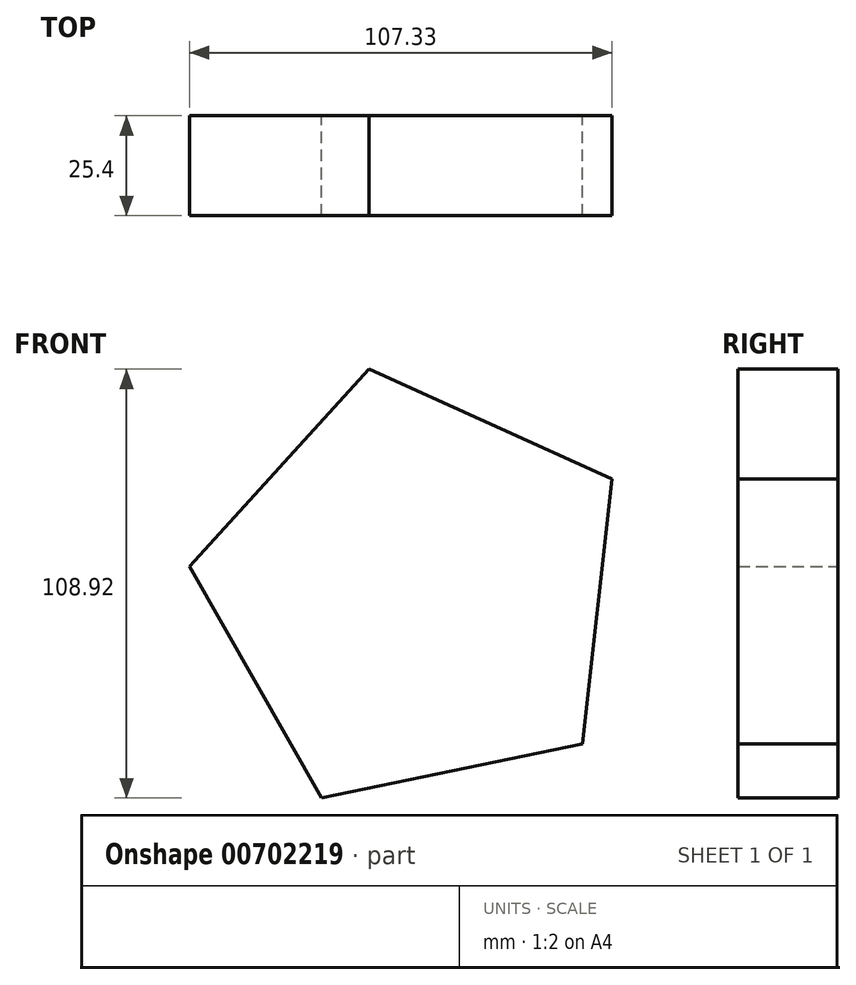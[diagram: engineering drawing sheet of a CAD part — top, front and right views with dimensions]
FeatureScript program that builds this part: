
annotation { "Feature Type Name" : "Feature", "Feature Type Description" : "" }
export const myFeature = defineFeature(function(context is Context, id is Id, definition is map)
    precondition{}
    {
        {
            var Q0;
            Q0=qCreatedBy(makeId("Front.planeOp"),FACE);
            var sketch = newSketch(context, id + "F0", { "sketchPlane" : qUnion([Q0])});
            skCircle(sketch, "E0.cCircle", {"center": v(0, 0) * mm, "radius": 46.61 * mm, "construction": true});
            skLineSegment(sketch, "E0.0", {"start": v(-57.27, 6.35) * mm, "end": v(-11.66, 56.42) * mm});
            skLineSegment(sketch, "E0.1", {"start": v(-11.66, 56.42) * mm, "end": v(50.06, 28.53) * mm});
            skLineSegment(sketch, "E0.2", {"start": v(50.06, 28.53) * mm, "end": v(42.6, -38.8) * mm});
            skLineSegment(sketch, "E0.3", {"start": v(42.6, -38.8) * mm, "end": v(-23.73, -52.5) * mm});
            skLineSegment(sketch, "E0.4", {"start": v(-23.73, -52.5) * mm, "end": v(-57.27, 6.35) * mm});
            skPoint(sketch, "E0.0.midPoint", {"position": v(-34.46, 31.38) * mm});
            skSolve(sketch);
        }
        {
            var Q0;
            Q0=makeQuery(id+"F0.imprint","IMPRINT",FACE,{"disambiguationData":[TD([[makeQuery(id+"F0.imprint","IMPRINT",EDGE,{"derivedFrom":sQuery(id+"F0.wireOp",EDGE,"E0.0")}),-1.0]])]});
            extrude(context, id + "F1", {"entities" : qUnion([Q0]), "depth" : 25.4 * mm, "offsetDistance" : 25.4 * mm});
        }
    });
